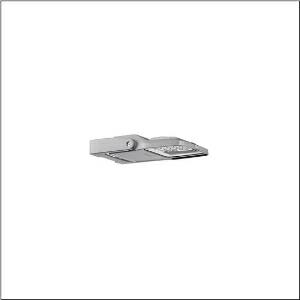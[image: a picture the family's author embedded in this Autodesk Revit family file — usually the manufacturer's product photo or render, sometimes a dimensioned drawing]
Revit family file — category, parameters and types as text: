
# Revit family: floodlight_fl_21_iq_micro___pl33t_5xa7761a4f2a_c8ff
name_source: partatom
category: Lighting Fixtures
units: mm (PartAtom-declared; Revit-internal decimal feet)

## family parameters
Cut with Voids When Loaded = No
Host = Face
Light Source = No
Part Type = Normal
Room Calculation Point = No
Round Connector Dimension = Use Diameter
Shared = No

## types (1)
- --- (1 x LED, 3050 lm, 23.1 W, 4000K)
    Apparent Load = 23 VA
    CIE Flux Codes = 26 75 99 100 100
    Color Rendering = 70
    Color Temperature = 4000K
    Default Elevation = 1800 mm
    Description = Floodlight FL 21 iQ micro, floodlight, primary light control with lens, of PMMA, primary optical cover: protective disc, of toughened safety glass, transparent, light distribution: PL33T, light emission: direct distribution, installation type: surface-mounted, LED, High Power LED, rated luminous flux: 3.050lm, luminous efficacy: 132lm/W, light colour: 740, colour temperature: 4000K, control gear: iQ Comfort/DALI, control: optimised constant luminous flux control (CLO 2.0), Desk-Remote (wireless, voltage-free reading and setting of iQ features in the workshop via application-optimized NFC function/RFID function), Light-Fading, Smart-Wire, Night-Set, Lumen-Switch, Temp-Guard, Auto-Match, with terminal, 6-pole, mains connection: 220..240V, AC, 50/60Hz, start of lifetime: 23W, end of service life: 24W, reduction: 11W, luminaire housing, of diecast aluminium, powder-coated, Siteco® metallic grey (DB 702S), corrosivity category C5 mid according to DIN EN ISO 12944, suitable for swimming pools, chlorine-resistant, sealing non-destructively replaceable, design bracket, of diecast aluminium, powder-coated, Siteco® metallic grey (DB 702S), protection rating (complete): IP66, insulation class (complete): insulation class II (safety insulation), certification: CE, ENEC, VDE, protection symbol: D, impact resistance: IK07, permissible operating ambient temperature: -40..+40°C, permissible operating ambient temperature for outdoor applications: -40..+50°C, standard: DIN EN 12944, LABS conformity tested according to VDMA 24364:2018-05, packaging unit: 1 piece

Light Distribution: PL33T
    Height = 65 mm
    Lamp = 1 x LED
    Lamp Light Flux = 3050 lm
    Lamp Power = 23.1 W
    Lamp count = 1
    Length = 312 mm
    Luminous efficacy = 132 lm/W
    Manufacturer = Siteco
    ModVariant = No
    Model = 5XA7761A4F2A
    Mounting Place = Wall
    Mounting Type = Surface mounted
    Number of Poles = 1
    OnlyDefault = Yes
    Power Factor = 1
    Product Name = Floodlight FL 21 iQ micro | PL33T
    Product group = floodlight | wall mounted
    ProductGroupID = 2001
    Protection Class = Protection class II
    Protection Degree = IP 66
    RLX_Detail_Level = 1
    RLX_Emergency_Light_Flux = 0 lm
    RLX_Emergency_Type = 0
    RLX_Emergency_Type_DB = No
    RlxData = <blob elided: 97321 chars, md5=beafecc8>
    Socket = socket
    Standby Power = 0 W
    System Light Flux = 3050 lm
    System Power = 23 W
    Type Comments = factory setting: luminous flux: 100 % | dim-lin: 254 | 455 mA
    Type Image = l_1006878.jpg
    URL = http://relux.com
    VarID = @adj_169587
    Voltage = 0 V
    Weight = 0.00 kg
    Width = 230 mm

## geometry (parser evidence)
native form markers: Blend x4, Sweep x14
no freeform markers — native parametric forms only
